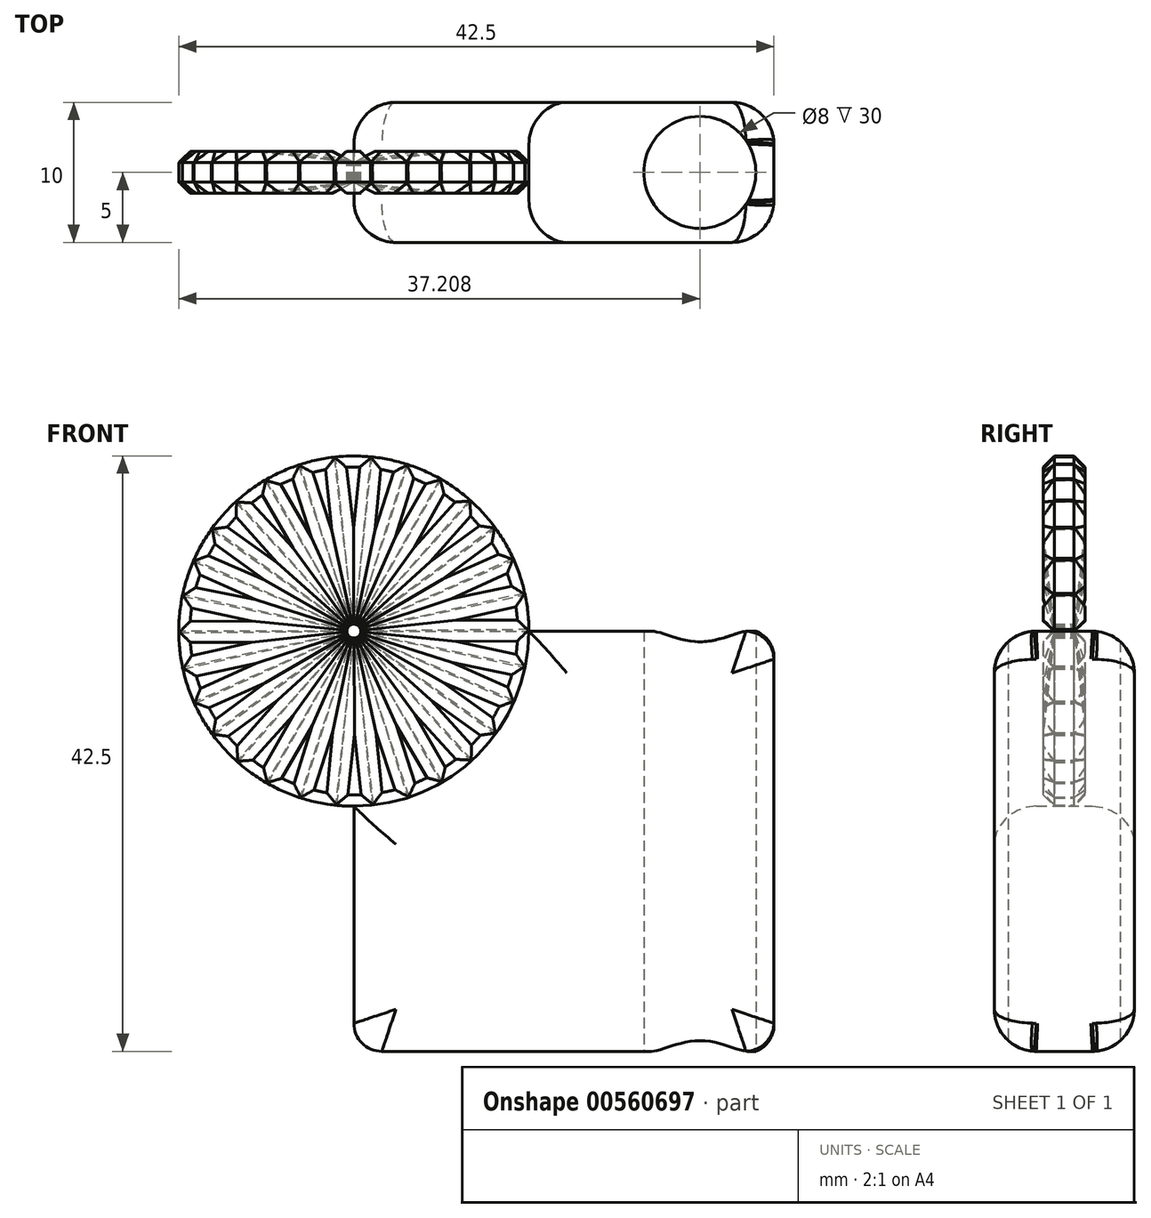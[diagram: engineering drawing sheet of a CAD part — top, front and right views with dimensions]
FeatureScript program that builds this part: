
annotation { "Feature Type Name" : "Feature", "Feature Type Description" : "" }
export const myFeature = defineFeature(function(context is Context, id is Id, definition is map)
    precondition{}
    {
        {
            var Q0;
            Q0=qCreatedBy(makeId("Front.planeOp"),FACE);
            var sketch = newSketch(context, id + "F0", { "sketchPlane" : qUnion([Q0])});
            skLineSegment(sketch, "E0.bottom", {"start": v(0, 0) * mm, "end": v(-30, 0) * mm});
            skLineSegment(sketch, "E0.top", {"start": v(0, 30) * mm, "end": v(-17.5, 30) * mm});
            skLineSegment(sketch, "E0.left", {"start": v(0, 0) * mm, "end": v(0, 30) * mm});
            skLineSegment(sketch, "E0.right", {"start": v(-30, 0) * mm, "end": v(-30, 17.5) * mm});
            skCircle(sketch, "E1", {"center": v(-30, 30) * mm, "radius": 12.5 * mm});
            skCircle(sketch, "E2", {"center": v(-30, 30) * mm, "radius": 0.5 * mm});
            skLineSegment(sketch, "E3", {"start": v(-30, 30) * mm, "end": v(-17.5, 30) * mm});
            skLineSegment(sketch, "E4", {"start": v(-30, 30) * mm, "end": v(-17.8, 32.7) * mm});
            skSolve(sketch);
        }
        {
            var Q0;
            Q0=makeQuery(id+"F0.imprint","IMPRINT",FACE,{"disambiguationData":[TD([[makeQuery(id+"F0.imprint","IMPRINT",EDGE,{"derivedFrom":sQuery(id+"F0.wireOp",EDGE,"E0.bottom")}),-1.0]])]});
            extrude(context, id + "F1", {"entities" : qUnion([Q0]), "endBound" : BoundingType.SYMMETRIC, "depth" : 10 * mm, "offsetDistance" : 25 * mm});
        }
        {
            var Q0;
            {var subQ0=sQuery(id+"F0.wireOp",EDGE,"E1");var subQ1=makeQuery(id+"F0.imprint","INTERSECT",VERTEX,{"derivedFrom":[sQuery(id+"F0.wireOp",EDGE,"E0.top"),subQ0]});Q0=makeQuery(id+"F0.imprint","IMPRINT",FACE,{"disambiguationData":[TD([[makeQuery(id+"F0.imprint","IMPRINT",EDGE,{"disambiguationData":[TD([[subQ1,-1.0]])],"derivedFrom":subQ0}),1.0]])]});}
            var Q1;
            {var subQ0=sQuery(id+"F0.wireOp",EDGE,"42352830-5f6b-481f-94b4-f665e785be34.1.0");Q1=makeQuery(id+"F0.imprint","IMPRINT",FACE,{"disambiguationData":[TD([[makeQuery(id+"F0.imprint","IMPRINT",EDGE,{"derivedFrom":subQ0}),1.0]])]});}
            var Q2;
            {var subQ0=sQuery(id+"F0.wireOp",EDGE,"42352830-5f6b-481f-94b4-f665e785be34.2.0");Q2=makeQuery(id+"F0.imprint","IMPRINT",FACE,{"disambiguationData":[TD([[makeQuery(id+"F0.imprint","IMPRINT",EDGE,{"derivedFrom":subQ0}),1.0]])]});}
            var Q3;
            {var subQ0=sQuery(id+"F0.wireOp",EDGE,"42352830-5f6b-481f-94b4-f665e785be34.3.0");Q3=makeQuery(id+"F0.imprint","IMPRINT",FACE,{"disambiguationData":[TD([[makeQuery(id+"F0.imprint","IMPRINT",EDGE,{"derivedFrom":subQ0}),1.0]])]});}
            var Q4;
            {var subQ0=sQuery(id+"F0.wireOp",EDGE,"42352830-5f6b-481f-94b4-f665e785be34.4.0");Q4=makeQuery(id+"F0.imprint","IMPRINT",FACE,{"disambiguationData":[TD([[makeQuery(id+"F0.imprint","IMPRINT",EDGE,{"derivedFrom":subQ0}),1.0]])]});}
            var Q5;
            {var subQ0=sQuery(id+"F0.wireOp",EDGE,"42352830-5f6b-481f-94b4-f665e785be34.5.0");Q5=makeQuery(id+"F0.imprint","IMPRINT",FACE,{"disambiguationData":[TD([[makeQuery(id+"F0.imprint","IMPRINT",EDGE,{"derivedFrom":subQ0}),1.0]])]});}
            var Q6;
            {var subQ0=sQuery(id+"F0.wireOp",EDGE,"42352830-5f6b-481f-94b4-f665e785be34.6.0");Q6=makeQuery(id+"F0.imprint","IMPRINT",FACE,{"disambiguationData":[TD([[makeQuery(id+"F0.imprint","IMPRINT",EDGE,{"derivedFrom":subQ0}),1.0]])]});}
            var Q7;
            {var subQ0=sQuery(id+"F0.wireOp",EDGE,"42352830-5f6b-481f-94b4-f665e785be34.7.0");Q7=makeQuery(id+"F0.imprint","IMPRINT",FACE,{"disambiguationData":[TD([[makeQuery(id+"F0.imprint","IMPRINT",EDGE,{"derivedFrom":subQ0}),1.0]])]});}
            var Q8;
            {var subQ0=sQuery(id+"F0.wireOp",EDGE,"42352830-5f6b-481f-94b4-f665e785be34.8.0");Q8=makeQuery(id+"F0.imprint","IMPRINT",FACE,{"disambiguationData":[TD([[makeQuery(id+"F0.imprint","IMPRINT",EDGE,{"derivedFrom":subQ0}),1.0]])]});}
            var Q9;
            {var subQ0=sQuery(id+"F0.wireOp",EDGE,"42352830-5f6b-481f-94b4-f665e785be34.9.0");Q9=makeQuery(id+"F0.imprint","IMPRINT",FACE,{"disambiguationData":[TD([[makeQuery(id+"F0.imprint","IMPRINT",EDGE,{"derivedFrom":subQ0}),1.0]])]});}
            var Q10;
            {var subQ0=sQuery(id+"F0.wireOp",EDGE,"42352830-5f6b-481f-94b4-f665e785be34.10.0");Q10=makeQuery(id+"F0.imprint","IMPRINT",FACE,{"disambiguationData":[TD([[makeQuery(id+"F0.imprint","IMPRINT",EDGE,{"derivedFrom":subQ0}),1.0]])]});}
            var Q11;
            {var subQ0=sQuery(id+"F0.wireOp",EDGE,"42352830-5f6b-481f-94b4-f665e785be34.11.0");Q11=makeQuery(id+"F0.imprint","IMPRINT",FACE,{"disambiguationData":[TD([[makeQuery(id+"F0.imprint","IMPRINT",EDGE,{"derivedFrom":subQ0}),1.0]])]});}
            var Q12;
            {var subQ0=sQuery(id+"F0.wireOp",EDGE,"42352830-5f6b-481f-94b4-f665e785be34.12.0");Q12=makeQuery(id+"F0.imprint","IMPRINT",FACE,{"disambiguationData":[TD([[makeQuery(id+"F0.imprint","IMPRINT",EDGE,{"derivedFrom":subQ0}),1.0]])]});}
            var Q13;
            {var subQ0=sQuery(id+"F0.wireOp",EDGE,"42352830-5f6b-481f-94b4-f665e785be34.13.0");Q13=makeQuery(id+"F0.imprint","IMPRINT",FACE,{"disambiguationData":[TD([[makeQuery(id+"F0.imprint","IMPRINT",EDGE,{"derivedFrom":subQ0}),1.0]])]});}
            var Q14;
            {var subQ0=sQuery(id+"F0.wireOp",EDGE,"42352830-5f6b-481f-94b4-f665e785be34.14.0");Q14=makeQuery(id+"F0.imprint","IMPRINT",FACE,{"disambiguationData":[TD([[makeQuery(id+"F0.imprint","IMPRINT",EDGE,{"derivedFrom":subQ0}),1.0]])]});}
            var Q15;
            {var subQ0=sQuery(id+"F0.wireOp",EDGE,"42352830-5f6b-481f-94b4-f665e785be34.15.0");Q15=makeQuery(id+"F0.imprint","IMPRINT",FACE,{"disambiguationData":[TD([[makeQuery(id+"F0.imprint","IMPRINT",EDGE,{"derivedFrom":subQ0}),1.0]])]});}
            var Q16;
            {var subQ0=sQuery(id+"F0.wireOp",EDGE,"42352830-5f6b-481f-94b4-f665e785be34.16.0");Q16=makeQuery(id+"F0.imprint","IMPRINT",FACE,{"disambiguationData":[TD([[makeQuery(id+"F0.imprint","IMPRINT",EDGE,{"derivedFrom":subQ0}),1.0]])]});}
            var Q17;
            {var subQ0=sQuery(id+"F0.wireOp",EDGE,"42352830-5f6b-481f-94b4-f665e785be34.17.0");Q17=makeQuery(id+"F0.imprint","IMPRINT",FACE,{"disambiguationData":[TD([[makeQuery(id+"F0.imprint","IMPRINT",EDGE,{"derivedFrom":subQ0}),1.0]])]});}
            var Q18;
            {var subQ0=sQuery(id+"F0.wireOp",EDGE,"42352830-5f6b-481f-94b4-f665e785be34.18.0");Q18=makeQuery(id+"F0.imprint","IMPRINT",FACE,{"disambiguationData":[TD([[makeQuery(id+"F0.imprint","IMPRINT",EDGE,{"derivedFrom":subQ0}),1.0]])]});}
            var Q19;
            {var subQ0=sQuery(id+"F0.wireOp",EDGE,"42352830-5f6b-481f-94b4-f665e785be34.19.0");Q19=makeQuery(id+"F0.imprint","IMPRINT",FACE,{"disambiguationData":[TD([[makeQuery(id+"F0.imprint","IMPRINT",EDGE,{"derivedFrom":subQ0}),1.0]])]});}
            var Q20;
            {var subQ0=sQuery(id+"F0.wireOp",EDGE,"42352830-5f6b-481f-94b4-f665e785be34.20.0");Q20=makeQuery(id+"F0.imprint","IMPRINT",FACE,{"disambiguationData":[TD([[makeQuery(id+"F0.imprint","IMPRINT",EDGE,{"derivedFrom":subQ0}),1.0]])]});}
            var Q21;
            {var subQ0=sQuery(id+"F0.wireOp",EDGE,"42352830-5f6b-481f-94b4-f665e785be34.21.0");Q21=makeQuery(id+"F0.imprint","IMPRINT",FACE,{"disambiguationData":[TD([[makeQuery(id+"F0.imprint","IMPRINT",EDGE,{"derivedFrom":subQ0}),1.0]])]});}
            var Q22;
            {var subQ2=sQuery(id+"F0.wireOp",EDGE,"42352830-5f6b-481f-94b4-f665e785be34.22.0");Q22=makeQuery(id+"F0.imprint","IMPRINT",FACE,{"disambiguationData":[TD([[makeQuery(id+"F0.imprint","IMPRINT",EDGE,{"derivedFrom":subQ2}),1.0]])]});}
            var Q23;
            {var subQ0=sQuery(id+"F0.wireOp",EDGE,"42352830-5f6b-481f-94b4-f665e785be34.23.0");Q23=makeQuery(id+"F0.imprint","IMPRINT",FACE,{"disambiguationData":[TD([[makeQuery(id+"F0.imprint","IMPRINT",EDGE,{"derivedFrom":subQ0}),1.0]])]});}
            var Q24;
            {var subQ0=sQuery(id+"F0.wireOp",EDGE,"42352830-5f6b-481f-94b4-f665e785be34.24.0");Q24=makeQuery(id+"F0.imprint","IMPRINT",FACE,{"disambiguationData":[TD([[makeQuery(id+"F0.imprint","IMPRINT",EDGE,{"derivedFrom":subQ0}),1.0]])]});}
            var Q25;
            {var subQ0=sQuery(id+"F0.wireOp",EDGE,"42352830-5f6b-481f-94b4-f665e785be34.25.0");Q25=makeQuery(id+"F0.imprint","IMPRINT",FACE,{"disambiguationData":[TD([[makeQuery(id+"F0.imprint","IMPRINT",EDGE,{"derivedFrom":subQ0}),1.0]])]});}
            var Q26;
            {var subQ0=sQuery(id+"F0.wireOp",EDGE,"42352830-5f6b-481f-94b4-f665e785be34.26.0");Q26=makeQuery(id+"F0.imprint","IMPRINT",FACE,{"disambiguationData":[TD([[makeQuery(id+"F0.imprint","IMPRINT",EDGE,{"derivedFrom":subQ0}),1.0]])]});}
            var Q27;
            {var subQ0=sQuery(id+"F0.wireOp",EDGE,"42352830-5f6b-481f-94b4-f665e785be34.28.0");Q27=makeQuery(id+"F0.imprint","IMPRINT",FACE,{"disambiguationData":[TD([[makeQuery(id+"F0.imprint","IMPRINT",EDGE,{"derivedFrom":subQ0}),1.0]])]});}
            var Q28;
            {var subQ0=sQuery(id+"F0.wireOp",EDGE,"qSf4lUen-YRTt-Okd2-AJCQ-30XvrwVoAf0U");Q28=makeQuery(id+"F0.imprint","IMPRINT",FACE,{"disambiguationData":[TD([[makeQuery(id+"F0.imprint","IMPRINT",EDGE,{"derivedFrom":subQ0}),-1.0]])]});}
            var Q29;
            {var subQ0=sQuery(id+"F0.wireOp",EDGE,"42352830-5f6b-481f-94b4-f665e785be34.27.0");Q29=makeQuery(id+"F0.imprint","IMPRINT",FACE,{"disambiguationData":[TD([[makeQuery(id+"F0.imprint","IMPRINT",EDGE,{"derivedFrom":subQ0}),1.0]])]});}
            extrude(context, id + "F2", {"entities" : qUnion([Q0, Q1, Q2, Q3, Q4, Q5, Q6, Q7, Q8, Q9, Q10, Q11, Q12, Q13, Q14, Q15, Q16, Q17, Q18, Q19, Q20, Q21, Q22, Q23, Q24, Q25, Q26, Q27, Q28, Q29]), "operationType" : NewBodyOperationType.ADD, "endBound" : BoundingType.SYMMETRIC, "depth" : 3 * mm, "offsetDistance" : 25 * mm});
        }
        {
            var Q0;
            Q0=makeQuery(id+"F2.opExtrude","CAP_EDGE",EDGE,{"disambiguationData":[OSD([sQuery(id+"F0.wireOp",EDGE,"E3")])],"isStart":false});
            var Q1;
            Q1=makeQuery(id+"F2.opExtrude","CAP_EDGE",EDGE,{"disambiguationData":[OSD([sQuery(id+"F0.wireOp",EDGE,"E4")])],"isStart":false});
            var Q2;
            Q2=makeQuery(id+"F2.opExtrude","CAP_EDGE",EDGE,{"disambiguationData":[OSD([sQuery(id+"F0.wireOp",EDGE,"E1")])],"isStart":false});
            var Q3;
            Q3=makeQuery(id+"F2.opExtrude","CAP_EDGE",EDGE,{"disambiguationData":[OSD([sQuery(id+"F0.wireOp",EDGE,"E3")])],"isStart":true});
            var Q4;
            Q4=makeQuery(id+"F2.opExtrude","CAP_EDGE",EDGE,{"disambiguationData":[OSD([sQuery(id+"F0.wireOp",EDGE,"E4")])],"isStart":true});
            var Q5;
            Q5=makeQuery(id+"F2.opExtrude","CAP_EDGE",EDGE,{"disambiguationData":[OSD([sQuery(id+"F0.wireOp",EDGE,"E1")])],"isStart":true});
            chamfer(context, id + "F3", {"entities" : qUnion([Q0, Q1, Q2, Q3, Q4, Q5]), "width" : 0.8 * mm, "tangentPropagation" : true});
        }
        {
            var Q0;
            Q0=qCreatedBy(makeId("Right.planeOp"),FACE);
            cPlane(context, id + "F4", {"entities" : qUnion([Q0]), "cplaneType" : CPlaneType.OFFSET, "offset" : 30 * mm, "oppositeDirection" : true, "width" : 150 * mm, "height" : 150 * mm});
        }
        {
            var Q0;
            Q0=qCreatedBy(id+"F4.planeOp",FACE);
            var sketch = newSketch(context, id + "F5", { "sketchPlane" : qUnion([Q0])});
            skLineSegment(sketch, "E5", {"start": v(6.42, 30) * mm, "end": v(-9.77, 30) * mm, "construction": true});
            skSolve(sketch);
        }
        {
            var Q0;
            Q0=makeQuery(id+"F2.opExtrude","SWEPT_BODY",BODY,{"disambiguationData":[OSD([sQuery(id+"F0.wireOp",EDGE,"E1"),sQuery(id+"F0.wireOp",EDGE,"z43yBgP8-4Rjq-ZQNF-UeEd-hYvT7gV5sddB"),sQuery(id+"F0.wireOp",EDGE,"cb6d640a-e941-445a-a836-e6fd786abb12.1.0")])]});
            var Q1;
            Q1=sQuery(id+"F5.wireOp",EDGE,"E5");
            circularPattern(context, id + "F6", {"entities" : qUnion([Q0]), "axis" : qUnion([Q1]), "angle" : 360 * degree, "instanceCount" : 30, "equalSpace" : true});
        }
        {
            var Q0;
            Q0=qCreatedBy(makeId("Top.planeOp"),FACE);
            var sketch = newSketch(context, id + "F7", { "sketchPlane" : qUnion([Q0])});
            skCircle(sketch, "E6", {"center": v(-5.3, 0) * mm, "radius": 4 * mm});
            skSolve(sketch);
        }
        {
            var Q0;
            Q0=makeQuery(id+"F7.imprint","IMPRINT",FACE,{"disambiguationData":[TD([[makeQuery(id+"F7.imprint","IMPRINT",EDGE,{"derivedFrom":sQuery(id+"F7.wireOp",EDGE,"E6")}),1.0]])]});
            extrude(context, id + "F8", {"entities" : qUnion([Q0]), "operationType" : NewBodyOperationType.REMOVE, "endBound" : BoundingType.THROUGH_ALL, "depth" : 25 * mm, "offsetDistance" : 25 * mm});
        }
        {
            var Q0;
            Q0=makeQuery(id+"F1.opExtrude","CAP_FACE",FACE,{"disambiguationData":[OSD([sQuery(id+"F0.wireOp",EDGE,"E0.bottom"),sQuery(id+"F0.wireOp",EDGE,"E0.top"),sQuery(id+"F0.wireOp",EDGE,"E0.left"),sQuery(id+"F0.wireOp",EDGE,"E0.right"),sQuery(id+"F0.wireOp",EDGE,"E1")])],"isStart":false});
            var Q1;
            Q1=makeQuery(id+"F1.opExtrude","CAP_FACE",FACE,{"disambiguationData":[OSD([sQuery(id+"F0.wireOp",EDGE,"E0.bottom"),sQuery(id+"F0.wireOp",EDGE,"E0.top"),sQuery(id+"F0.wireOp",EDGE,"E0.left"),sQuery(id+"F0.wireOp",EDGE,"E0.right"),sQuery(id+"F0.wireOp",EDGE,"E1")])],"isStart":true});
            fillet(context, id + "F9", {"entities" : qUnion([Q0, Q1]), "radius" : 3 * mm, "tangentPropagation" : true, "allowEdgeOverflow" : false});
        }
        {
            var Q0;
            Q0=makeQuery(id+"F1.opExtrude","SWEPT_EDGE",EDGE,{"disambiguationData":[OSD([sQuery(id+"F0.wireOp",EDGE,"E0.top"),sQuery(id+"F0.wireOp",EDGE,"E0.left")])]});
            var Q1;
            Q1=makeQuery(id+"F1.opExtrude","SWEPT_EDGE",EDGE,{"disambiguationData":[OSD([sQuery(id+"F0.wireOp",EDGE,"E0.bottom"),sQuery(id+"F0.wireOp",EDGE,"E0.left")])]});
            var Q2;
            Q2=makeQuery(id+"F1.opExtrude","SWEPT_EDGE",EDGE,{"disambiguationData":[OSD([sQuery(id+"F0.wireOp",EDGE,"E0.bottom"),sQuery(id+"F0.wireOp",EDGE,"E0.right")])]});
            fillet(context, id + "F10", {"entities" : qUnion([Q0, Q1, Q2]), "radius" : 2 * mm, "tangentPropagation" : true, "allowEdgeOverflow" : false});
        }
    });
